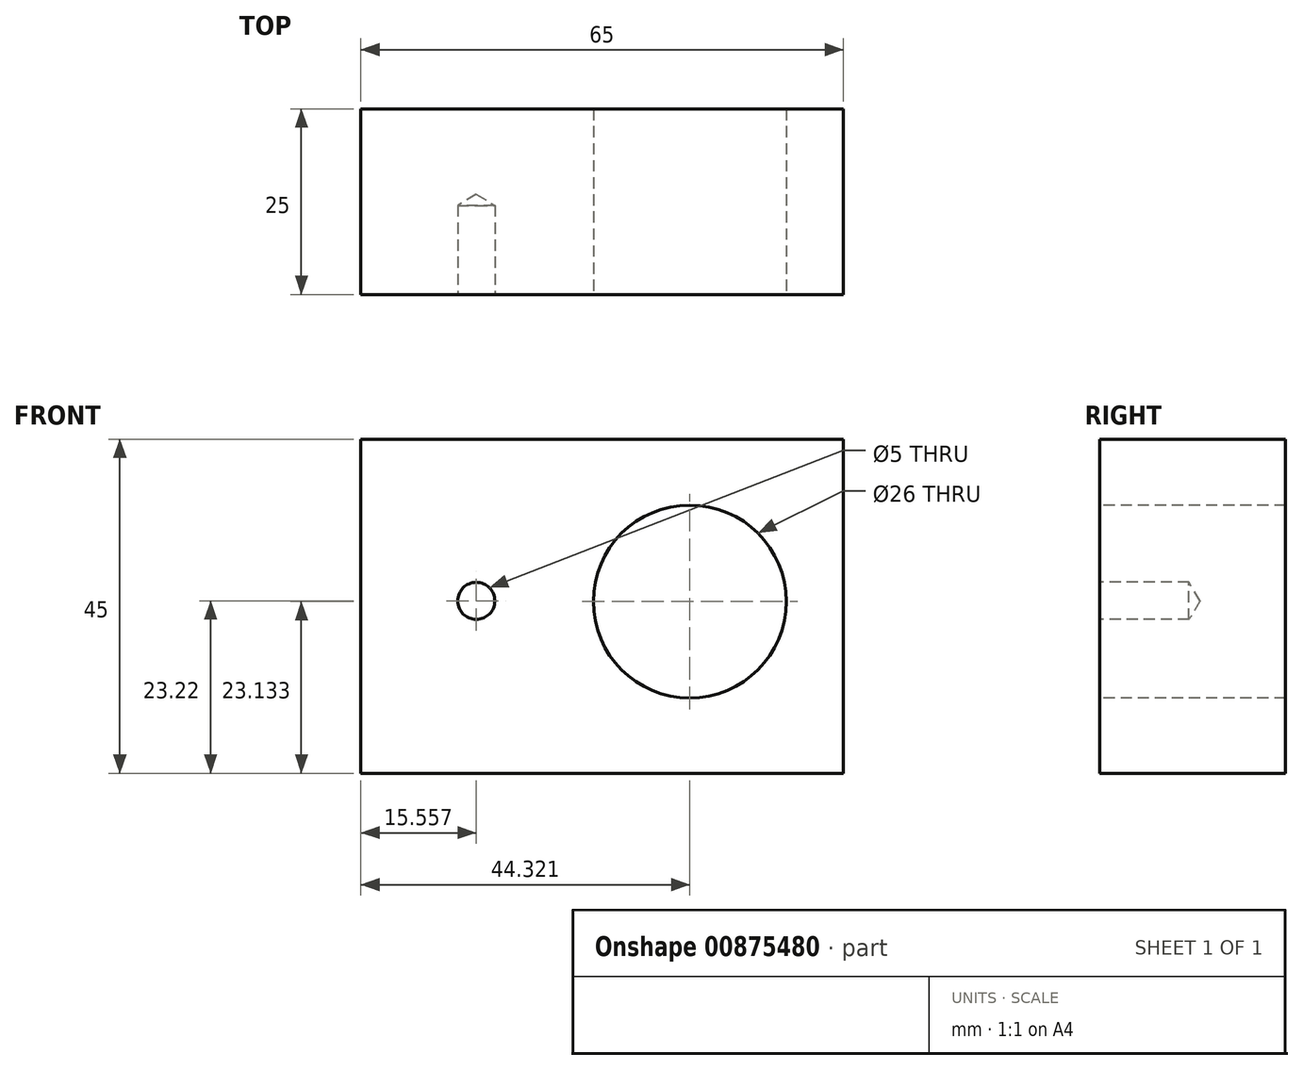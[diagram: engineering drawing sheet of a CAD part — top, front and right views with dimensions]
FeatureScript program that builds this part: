
annotation { "Feature Type Name" : "Feature", "Feature Type Description" : "" }
export const myFeature = defineFeature(function(context is Context, id is Id, definition is map)
    precondition{}
    {
        {
            var Q0;
            Q0=qCreatedBy(makeId("Front.planeOp"),FACE);
            var sketch = newSketch(context, id + "F0", { "sketchPlane" : qUnion([Q0])});
            skLineSegment(sketch, "E0.bottom", {"start": v(-33.63, 21.78) * mm, "end": v(31.37, 21.78) * mm});
            skLineSegment(sketch, "E0.top", {"start": v(-33.63, -23.22) * mm, "end": v(31.37, -23.22) * mm});
            skLineSegment(sketch, "E0.left", {"start": v(-33.63, 21.78) * mm, "end": v(-33.63, -23.22) * mm});
            skLineSegment(sketch, "E0.right", {"start": v(31.37, 21.78) * mm, "end": v(31.37, -23.22) * mm});
            skSolve(sketch);
        }
        {
            var Q0;
            Q0=makeQuery(id+"F0.imprint","IMPRINT",FACE,{"disambiguationData":[TD([[makeQuery(id+"F0.imprint","IMPRINT",EDGE,{"derivedFrom":sQuery(id+"F0.wireOp",EDGE,"E0.bottom")}),-1.0]])]});
            extrude(context, id + "F1", {"entities" : qUnion([Q0]), "depth" : 25 * mm, "offsetDistance" : 25 * mm});
        }
        {
            var Q0;
            Q0=makeQuery(id+"F1.opExtrude","CAP_FACE",FACE,{"disambiguationData":[OSD([sQuery(id+"F0.wireOp",EDGE,"E0.bottom"),sQuery(id+"F0.wireOp",EDGE,"E0.top"),sQuery(id+"F0.wireOp",EDGE,"E0.left"),sQuery(id+"F0.wireOp",EDGE,"E0.right")])],"isStart":false});
            var sketch = newSketch(context, id + "F2", { "sketchPlane" : qUnion([Q0])});
            skCircle(sketch, "E1", {"center": v(-18.07, 0) * mm, "radius": 7 * mm});
            skSolve(sketch);
        }
        {
            var Q0;
            Q0=sQuery(id+"F2.wireOp",VERTEX,"E1.center");
            var Q1;
            Q1=makeQuery(id+"F1.opExtrude","SWEPT_BODY",BODY,{"disambiguationData":[OSD([sQuery(id+"F0.wireOp",EDGE,"E0.bottom"),sQuery(id+"F0.wireOp",EDGE,"E0.top"),sQuery(id+"F0.wireOp",EDGE,"E0.left"),sQuery(id+"F0.wireOp",EDGE,"E0.right")])]});
            hole(context, id + "F3", {"style" : HoleStyle.SIMPLE, "endStyle" : HoleEndStyle.BLIND, "holeDiameter" : 5 * mm, "majorDiameter" : 5 * mm, "holeDepth" : 12 * mm, "isTappedThrough" : true, "tappedDepth" : 12 * mm, "tapClearance" : 3, "startFromSketch" : true, "locations" : qUnion([Q0]), "scope" : qUnion([Q1])});
        }
        {
            var Q0;
            Q0=makeQuery(id+"F1.opExtrude","CAP_FACE",FACE,{"disambiguationData":[OSD([sQuery(id+"F0.wireOp",EDGE,"E0.bottom"),sQuery(id+"F0.wireOp",EDGE,"E0.top"),sQuery(id+"F0.wireOp",EDGE,"E0.left"),sQuery(id+"F0.wireOp",EDGE,"E0.right")])],"isStart":false});
            var sketch = newSketch(context, id + "F4", { "sketchPlane" : qUnion([Q0])});
            skCircle(sketch, "E2", {"center": v(10.7, -0.09) * mm, "radius": 13 * mm});
            skSolve(sketch);
        }
        {
            var Q0;
            Q0=makeQuery(id+"F4.imprint","IMPRINT",FACE,{"disambiguationData":[TD([[makeQuery(id+"F4.imprint","IMPRINT",EDGE,{"derivedFrom":sQuery(id+"F4.wireOp",EDGE,"E2")}),1.0]])]});
            extrude(context, id + "F5", {"entities" : qUnion([Q0]), "operationType" : NewBodyOperationType.REMOVE, "endBound" : BoundingType.THROUGH_ALL, "oppositeDirection" : true, "depth" : 25 * mm, "offsetDistance" : 25 * mm});
        }
    });
